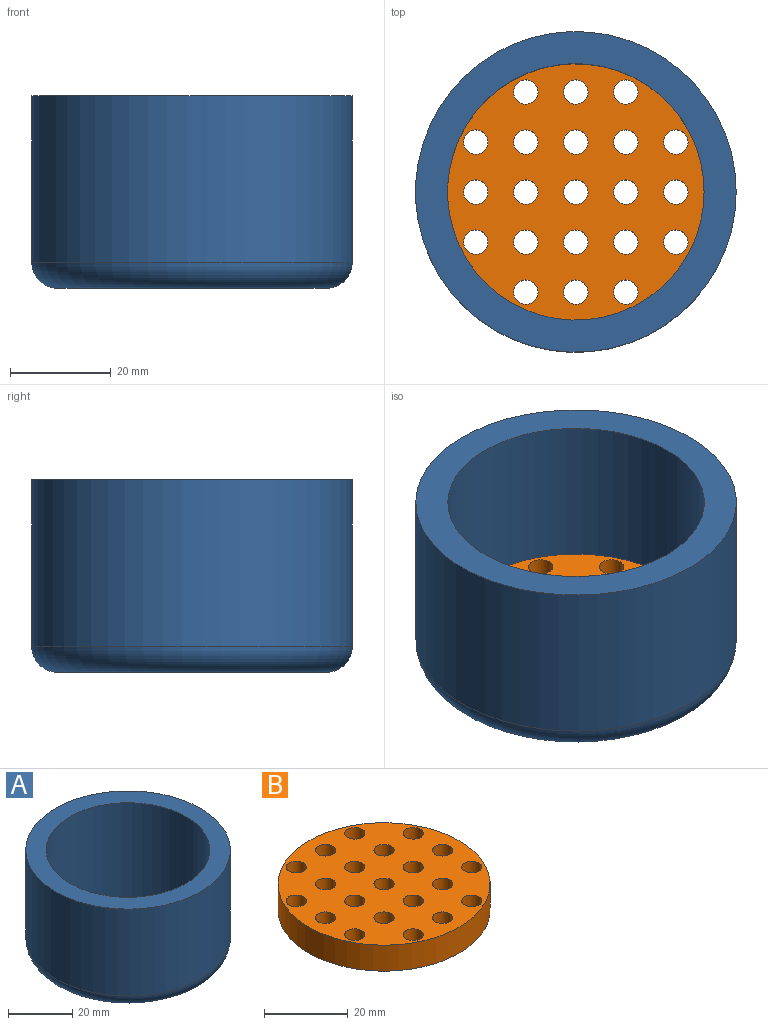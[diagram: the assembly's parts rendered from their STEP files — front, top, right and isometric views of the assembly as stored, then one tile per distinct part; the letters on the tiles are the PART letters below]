
ASSEMBLY  parts=2 mates=1
PART A: 5 faces, bbox 68.7x68.7x38.1 mm
  f0: cylinder r=31.75mm len=63.5mm, axis (0,0,-1), area 6587.2mm2, adj f1,f4
  f1: plane 63.5x63.5mm, normal (0,0,1), area 1140.1mm2, adj f0,f3
  f2: plane 53.34x53.34mm, normal (0,0,-1), area 207.8mm2, adj f3,f4
  f3: cylinder r=25.4mm len=50.8mm, axis (0,0,1), area 6080.5mm2, adj f1,f2
  f4: torus R=26.67mm, axis (0,0,1), area 1499.3mm2, adj f0,f2
PART B: 24 faces, bbox 50.8x50.8x7.6 mm
  f0: cylinder r=2.41mm len=7.62mm, axis (0,0,-1), area 115.5mm2, adj f22,f23
  f1: cylinder r=2.41mm len=7.62mm, axis (0,0,-1), area 115.5mm2, adj f22,f23
  f2: cylinder r=2.41mm len=7.62mm, axis (0,0,-1), area 115.5mm2, adj f22,f23
  f3: cylinder r=2.41mm len=7.62mm, axis (0,0,-1), area 115.5mm2, adj f22,f23
  f4: cylinder r=2.41mm len=7.62mm, axis (0,0,-1), area 115.5mm2, adj f22,f23
  f5: cylinder r=2.41mm len=7.62mm, axis (0,0,-1), area 115.5mm2, adj f22,f23
  f6: cylinder r=2.41mm len=7.62mm, axis (0,0,-1), area 115.5mm2, adj f22,f23
  f7: cylinder r=2.41mm len=7.62mm, axis (0,0,-1), area 115.5mm2, adj f22,f23
  f8: cylinder r=2.41mm len=7.62mm, axis (0,0,-1), area 115.5mm2, adj f22,f23
  f9: cylinder r=2.41mm len=7.62mm, axis (0,0,-1), area 115.5mm2, adj f22,f23
  f10: cylinder r=2.41mm len=7.62mm, axis (0,0,-1), area 115.5mm2, adj f22,f23
  f11: cylinder r=2.41mm len=7.62mm, axis (0,0,-1), area 115.5mm2, adj f22,f23
  f12: cylinder r=2.41mm len=7.62mm, axis (0,0,-1), area 115.5mm2, adj f22,f23
  f13: cylinder r=2.41mm len=7.62mm, axis (0,0,-1), area 115.5mm2, adj f22,f23
  f14: cylinder r=2.41mm len=7.62mm, axis (0,0,-1), area 115.5mm2, adj f22,f23
  f15: cylinder r=2.41mm len=7.62mm, axis (0,0,-1), area 115.5mm2, adj f22,f23
  f16: cylinder r=2.41mm len=7.62mm, axis (0,0,-1), area 115.5mm2, adj f22,f23
  f17: cylinder r=2.41mm len=7.62mm, axis (0,0,-1), area 115.5mm2, adj f22,f23
  f18: cylinder r=2.41mm len=7.62mm, axis (0,0,-1), area 115.5mm2, adj f22,f23
  f19: cylinder r=2.41mm len=7.62mm, axis (0,0,-1), area 115.5mm2, adj f22,f23
  f20: cylinder r=2.41mm len=7.62mm, axis (0,0,-1), area 115.5mm2, adj f22,f23
  f21: cylinder r=25.4mm len=50.8mm, axis (0,0,-1), area 1216.1mm2, adj f22,f23
  f22: plane 50.8x50.8mm, normal (0,0,1), area 1642.7mm2, adj f0,f1,f2,f3,f4,f5,f6,f7
  f23: plane 50.8x50.8mm, normal (0,0,-1), area 1642.7mm2, adj f0,f1,f2,f3,f4,f5,f6,f7
PLACE A t=(-4.48,-2.44,-18.83)mm
PLACE B t=(-4.48,-2.44,-18.83)mm
MATE fastened B.f21 <-> A.f3  axis (0,0,-1) through (-4.48,-2.44,-18.83)mm
